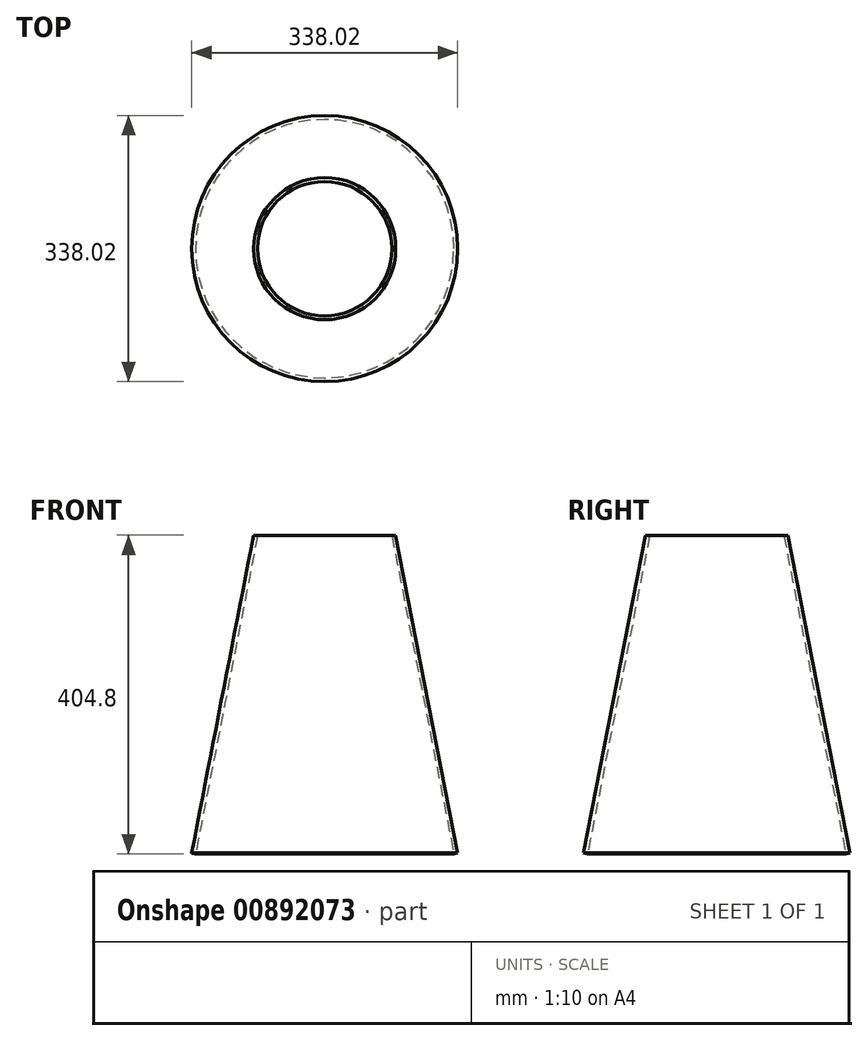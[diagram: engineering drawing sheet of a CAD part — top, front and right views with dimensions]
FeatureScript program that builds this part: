
annotation { "Feature Type Name" : "Feature", "Feature Type Description" : "" }
export const myFeature = defineFeature(function(context is Context, id is Id, definition is map)
    precondition{}
    {
        {
            var Q0;
            Q0=qCreatedBy(makeId("Front.planeOp"),FACE);
            var sketch = newSketch(context, id + "F0", { "sketchPlane" : qUnion([Q0])});
            skLineSegment(sketch, "E0", {"start": v(0, 0) * mm, "end": v(0, 502.34) * mm, "construction": true});
            skLineSegment(sketch, "E1", {"start": v(164.1, 58) * mm, "end": v(85.35, 461.84) * mm});
            skLineSegment(sketch, "E2", {"start": v(164.1, 58) * mm, "end": v(169, 58.96) * mm});
            skLineSegment(sketch, "E3", {"start": v(169, 58.96) * mm, "end": v(90.26, 462.8) * mm});
            skLineSegment(sketch, "E4", {"start": v(85.35, 461.84) * mm, "end": v(90.26, 462.8) * mm});
            skSolve(sketch);
        }
        {
            var Q0;
            Q0=makeQuery(id+"F0.imprint","IMPRINT",FACE,{"disambiguationData":[TD([[makeQuery(id+"F0.imprint","IMPRINT",EDGE,{"derivedFrom":sQuery(id+"F0.wireOp",EDGE,"E1")}),-1.0]])]});
            var Q1;
            Q1=sQuery(id+"F0.wireOp",EDGE,"E0");
            revolve(context, id + "F1", {"entities" : qUnion([Q0]), "axis" : qUnion([Q1]), "revolveType" : RevolveType.FULL});
        }
    });
